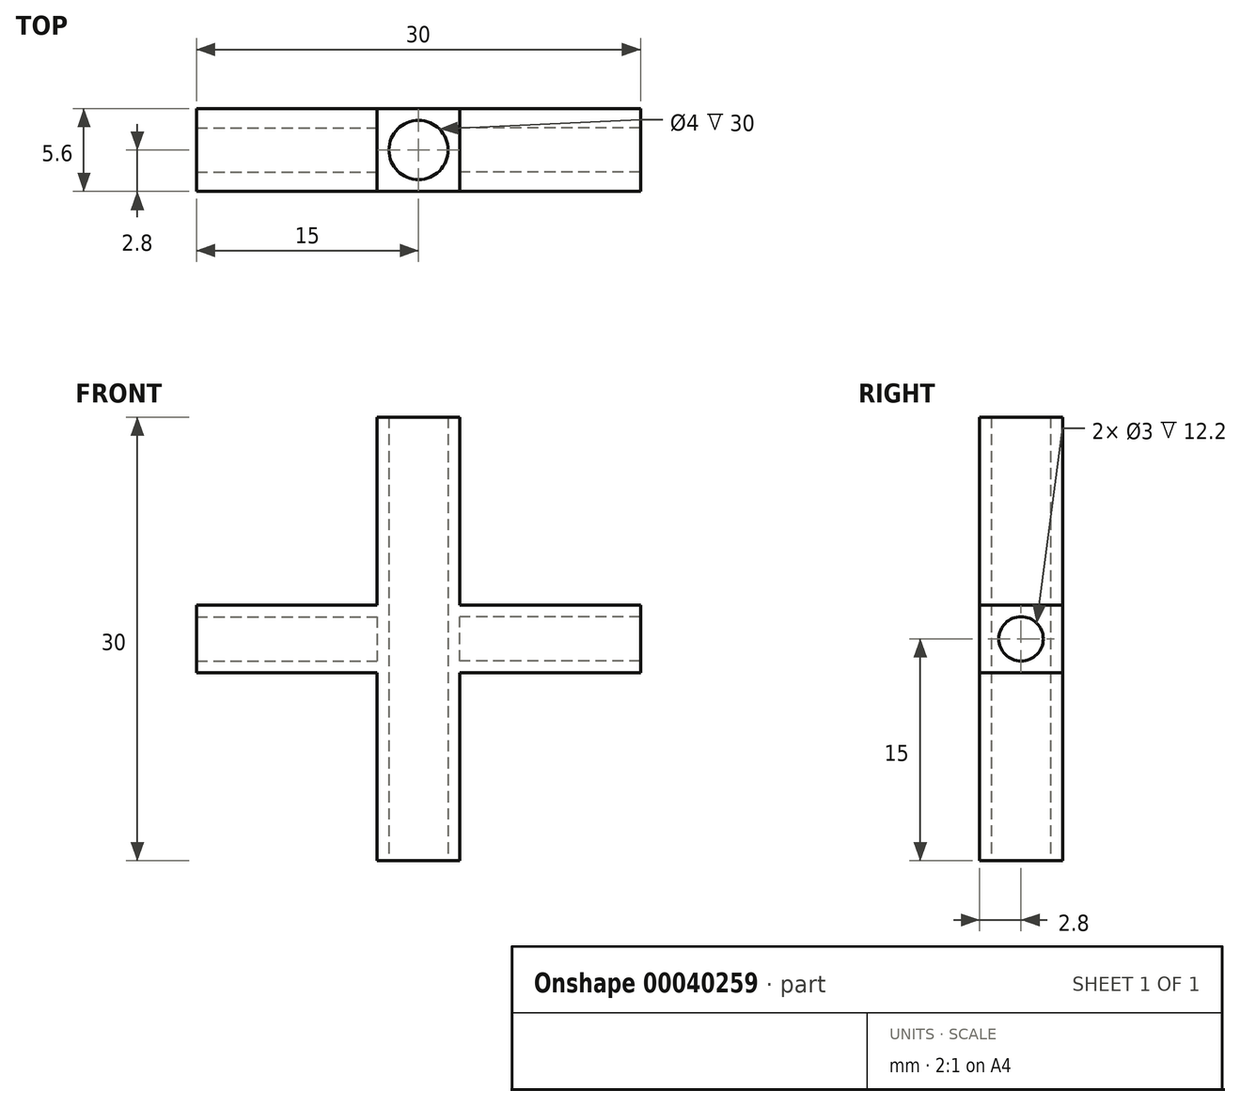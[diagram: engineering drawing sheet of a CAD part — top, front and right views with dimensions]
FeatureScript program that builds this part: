
annotation { "Feature Type Name" : "Feature", "Feature Type Description" : "" }
export const myFeature = defineFeature(function(context is Context, id is Id, definition is map)
    precondition{}
    {
        {
            var Q0;
            Q0=qCreatedBy(makeId("Top.planeOp"),FACE);
            var sketch = newSketch(context, id + "F0", { "sketchPlane" : qUnion([Q0])});
            skCircle(sketch, "E0", {"center": v(0, 0) * mm, "radius": 2 * mm});
            skLineSegment(sketch, "E1.bottom", {"start": v(-2.8, 2.8) * mm, "end": v(2.8, 2.8) * mm});
            skLineSegment(sketch, "E1.top", {"start": v(-2.8, -2.8) * mm, "end": v(2.8, -2.8) * mm});
            skLineSegment(sketch, "E1.left", {"start": v(-2.8, 2.8) * mm, "end": v(-2.8, -2.8) * mm});
            skLineSegment(sketch, "E1.right", {"start": v(2.8, 2.8) * mm, "end": v(2.8, -2.8) * mm});
            skSolve(sketch);
        }
        {
            var Q0;
            Q0=makeQuery(id+"F0.imprint","IMPRINT",FACE,{"disambiguationData":[TD([[makeQuery(id+"F0.imprint","IMPRINT",EDGE,{"derivedFrom":sQuery(id+"F0.wireOp",EDGE,"E0")}),-1.0]])]});
            extrude(context, id + "F1", {"entities" : qUnion([Q0]), "depth" : 30 * mm});
        }
        {
            var Q0;
            Q0=makeQuery(id+"F1.opExtrude","SWEPT_FACE",FACE,{"disambiguationData":[OSD([sQuery(id+"F0.wireOp",EDGE,"E1.right")])]});
            var sketch = newSketch(context, id + "F2", { "sketchPlane" : qUnion([Q0])});
            skPoint(sketch, "E2", {"position": v(2.8, 15) * mm});
            skPoint(sketch, "E3", {"position": v(-2.8, 15) * mm});
            skPoint(sketch, "E4", {"position": v(0, 15) * mm});
            skCircle(sketch, "E5", {"center": v(0, 15) * mm, "radius": 1.5 * mm});
            skLineSegment(sketch, "E6", {"start": v(2.8, 17.3) * mm, "end": v(-2.8, 17.3) * mm});
            skLineSegment(sketch, "E7", {"start": v(-2.8, 12.7) * mm, "end": v(2.8, 12.7) * mm});
            skSolve(sketch);
        }
        {
            var Q0;
            Q0=makeQuery(id+"F2.imprint","IMPRINT",FACE,{"disambiguationData":[TD([[makeQuery(id+"F2.imprint","IMPRINT",EDGE,{"derivedFrom":sQuery(id+"F2.wireOp",EDGE,"E5")}),-1.0]])]});
            extrude(context, id + "F3", {"entities" : qUnion([Q0]), "operationType" : NewBodyOperationType.ADD, "depth" : 12.2 * mm});
        }
        {
            var Q0;
            Q0=makeQuery(id+"F1.opExtrude","SWEPT_FACE",FACE,{"disambiguationData":[OSD([sQuery(id+"F0.wireOp",EDGE,"E1.left")])]});
            var sketch = newSketch(context, id + "F4", { "sketchPlane" : qUnion([Q0])});
            skPoint(sketch, "E8", {"position": v(-2.8, 15) * mm});
            skPoint(sketch, "E9", {"position": v(2.8, 15) * mm});
            skPoint(sketch, "E10", {"position": v(0, 15) * mm});
            skCircle(sketch, "E11", {"center": v(0, 15) * mm, "radius": 1.5 * mm});
            skLineSegment(sketch, "E12", {"start": v(-2.8, 12.7) * mm, "end": v(2.8, 12.7) * mm});
            skLineSegment(sketch, "E13", {"start": v(-2.8, 17.3) * mm, "end": v(2.8, 17.3) * mm});
            skSolve(sketch);
        }
        {
            var Q0;
            Q0=makeQuery(id+"F4.imprint","IMPRINT",FACE,{"disambiguationData":[TD([[makeQuery(id+"F4.imprint","IMPRINT",EDGE,{"derivedFrom":sQuery(id+"F4.wireOp",EDGE,"E11")}),-1.0]])]});
            extrude(context, id + "F5", {"entities" : qUnion([Q0]), "operationType" : NewBodyOperationType.ADD, "depth" : 12.2 * mm});
        }
    });
